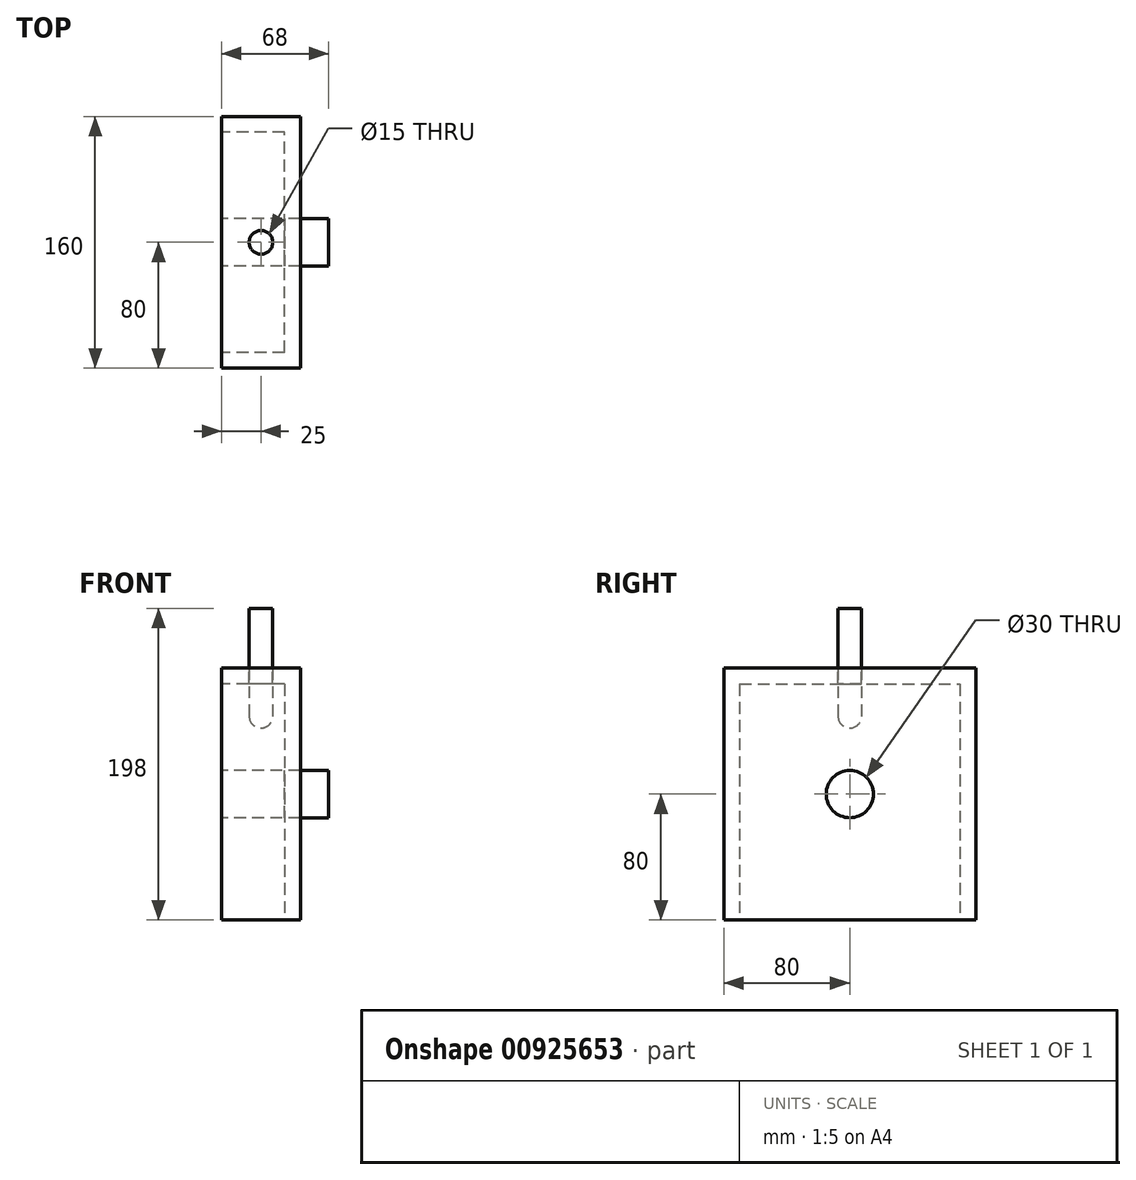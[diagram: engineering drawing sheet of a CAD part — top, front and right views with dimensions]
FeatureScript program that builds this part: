
annotation { "Feature Type Name" : "Feature", "Feature Type Description" : "" }
export const myFeature = defineFeature(function(context is Context, id is Id, definition is map)
    precondition{}
    {
        {
            var Q0;
            Q0=qCreatedBy(makeId("Right.planeOp"),FACE);
            var sketch = newSketch(context, id + "F0", { "sketchPlane" : qUnion([Q0])});
            skLineSegment(sketch, "E0.bottom", {"start": v(-80, 0) * mm, "end": v(80, 0) * mm});
            skLineSegment(sketch, "E0.top", {"start": v(-80, -160) * mm, "end": v(80, -160) * mm});
            skLineSegment(sketch, "E0.left", {"start": v(-80, 0) * mm, "end": v(-80, -160) * mm});
            skLineSegment(sketch, "E0.right", {"start": v(80, 0) * mm, "end": v(80, -160) * mm});
            skCircle(sketch, "E1", {"center": v(0, -80) * mm, "radius": 15 * mm});
            skSolve(sketch);
        }
        {
            var Q0;
            Q0=makeQuery(id+"F0.imprint","IMPRINT",FACE,{"disambiguationData":[TD([[makeQuery(id+"F0.imprint","IMPRINT",EDGE,{"derivedFrom":sQuery(id+"F0.wireOp",EDGE,"E0.bottom")}),-1.0]])]});
            var Q1;
            Q1=makeQuery(id+"F0.imprint","IMPRINT",FACE,{"disambiguationData":[TD([[makeQuery(id+"F0.imprint","IMPRINT",EDGE,{"derivedFrom":sQuery(id+"F0.wireOp",EDGE,"E1")}),1.0]])]});
            extrude(context, id + "F1", {"entities" : qUnion([Q0, Q1]), "depth" : 50 * mm, "offsetDistance" : 25 * mm});
        }
        {
            var Q0;
            Q0=makeQuery(id+"F1.opExtrude","SWEPT_FACE",FACE,{"disambiguationData":[OSD([sQuery(id+"F0.wireOp",EDGE,"E0.top")])]});
            var Q1;
            Q1=makeQuery(id+"F1.opExtrude","CAP_FACE",FACE,{"disambiguationData":[OSD([sQuery(id+"F0.wireOp",EDGE,"E0.bottom"),sQuery(id+"F0.wireOp",EDGE,"E0.top"),sQuery(id+"F0.wireOp",EDGE,"E0.left"),sQuery(id+"F0.wireOp",EDGE,"E0.right")])],"isStart":true});
            shell(context, id + "F2", {"entities" : qUnion([Q0, Q1]), "thickness" : 10 * mm});
        }
        {
            var Q0;
            Q0=makeQuery(id+"F0.imprint","IMPRINT",FACE,{"disambiguationData":[TD([[makeQuery(id+"F0.imprint","IMPRINT",EDGE,{"derivedFrom":sQuery(id+"F0.wireOp",EDGE,"E1")}),1.0]])]});
            extrude(context, id + "F3", {"entities" : qUnion([Q0]), "operationType" : NewBodyOperationType.REMOVE, "depth" : 65 * mm, "offsetDistance" : 25 * mm});
        }
        {
            var Q0;
            Q0=makeQuery(id+"F1.opExtrude","SWEPT_FACE",FACE,{"disambiguationData":[OSD([sQuery(id+"F0.wireOp",EDGE,"E0.bottom")])]});
            var sketch = newSketch(context, id + "F4", { "sketchPlane" : qUnion([Q0])});
            skCircle(sketch, "E2", {"center": v(25, 0) * mm, "radius": 7.5 * mm});
            skPoint(sketch, "E2.centerSnap0", {"position": v(25, -80) * mm});
            skSolve(sketch);
        }
        {
            var Q0;
            Q0=makeQuery(id+"F4.imprint","IMPRINT",FACE,{"disambiguationData":[TD([[makeQuery(id+"F4.imprint","IMPRINT",EDGE,{"derivedFrom":sQuery(id+"F4.wireOp",EDGE,"E2")}),1.0]])]});
            extrude(context, id + "F5", {"entities" : qUnion([Q0]), "operationType" : NewBodyOperationType.REMOVE, "oppositeDirection" : true, "depth" : 35 * mm, "offsetDistance" : 25 * mm});
        }
        {
            var Q0;
            Q0=makeQuery(id+"F4.imprint","IMPRINT",FACE,{"disambiguationData":[TD([[makeQuery(id+"F4.imprint","IMPRINT",EDGE,{"derivedFrom":sQuery(id+"F4.wireOp",EDGE,"E2")}),1.0]])]});
            extrude(context, id + "F6", {"entities" : qUnion([Q0]), "depth" : 76 * mm, "offsetDistance" : 25 * mm, "symmetric" : true});
        }
        {
            var Q0;
            Q0=makeQuery(id+"F6.opExtrude","CAP_EDGE",EDGE,{"disambiguationData":[OSD([sQuery(id+"F4.wireOp",EDGE,"E2")])],"isStart":true});
            fillet(context, id + "F7", {"entities" : qUnion([Q0]), "radius" : 7.5 * mm, "tangentPropagation" : true, "allowEdgeOverflow" : false});
        }
        {
            var Q0;
            Q0=makeQuery(id+"F0.imprint","IMPRINT",FACE,{"disambiguationData":[TD([[makeQuery(id+"F0.imprint","IMPRINT",EDGE,{"derivedFrom":sQuery(id+"F0.wireOp",EDGE,"E1")}),1.0]])]});
            extrude(context, id + "F8", {"entities" : qUnion([Q0]), "depth" : 68 * mm, "offsetDistance" : 25 * mm});
        }
    });
